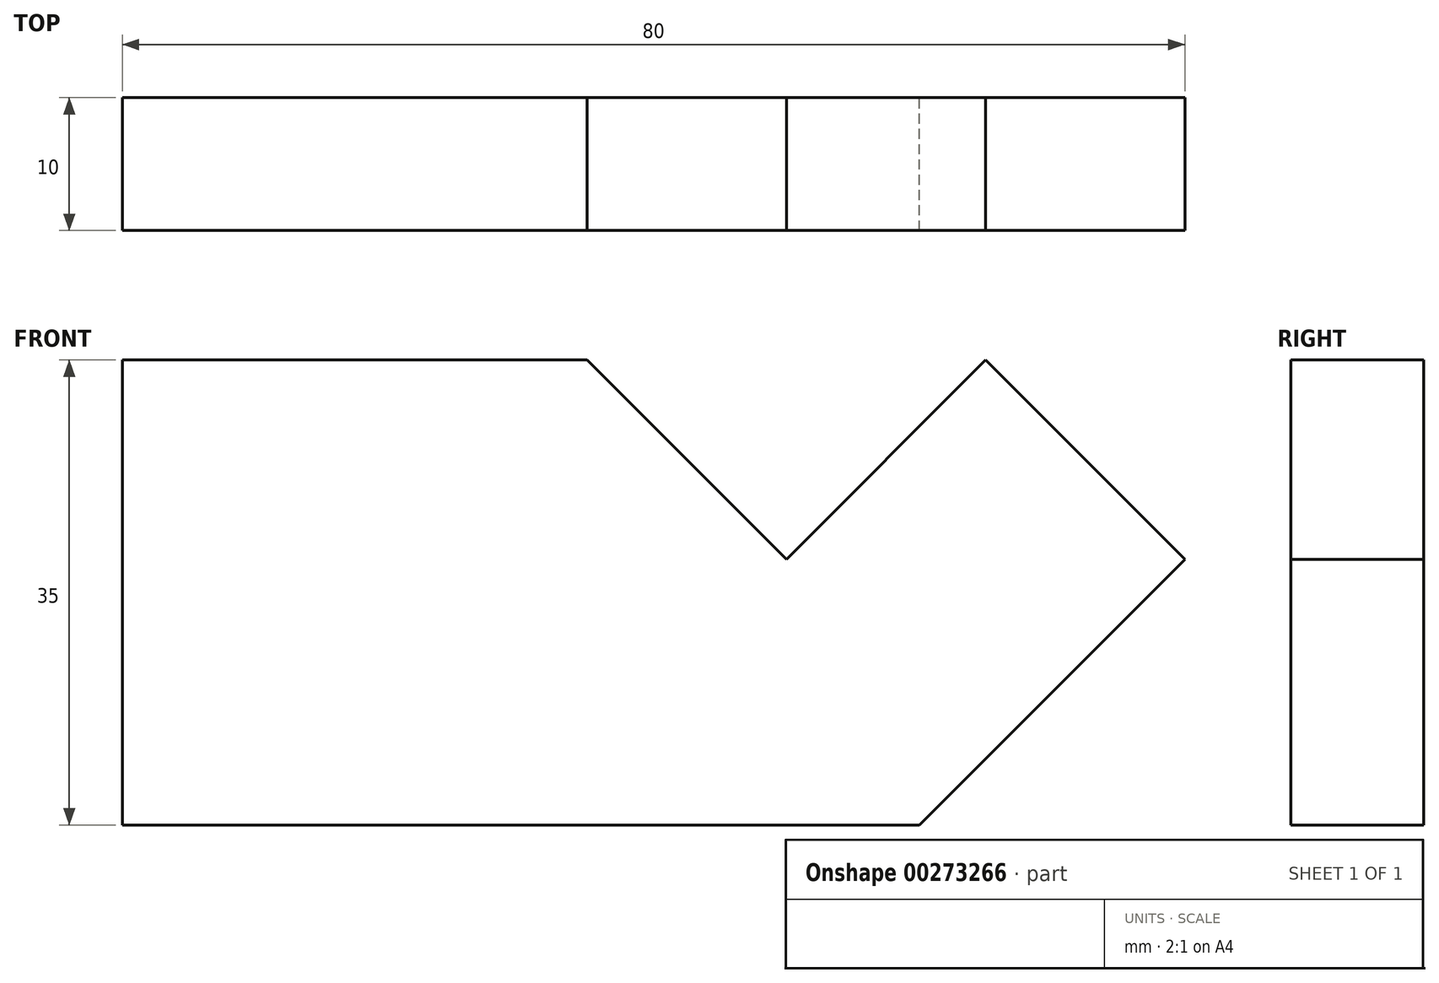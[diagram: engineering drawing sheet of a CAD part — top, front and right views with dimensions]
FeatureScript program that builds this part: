
annotation { "Feature Type Name" : "Feature", "Feature Type Description" : "" }
export const myFeature = defineFeature(function(context is Context, id is Id, definition is map)
    precondition{}
    {
        {
            var Q0;
            Q0=qCreatedBy(makeId("Front.planeOp"),FACE);
            var sketch = newSketch(context, id + "F0", { "sketchPlane" : qUnion([Q0])});
            skLineSegment(sketch, "E0", {"start": v(0, 0) * mm, "end": v(0, 35) * mm});
            skLineSegment(sketch, "E1", {"start": v(0, 35) * mm, "end": v(35, 35) * mm});
            skLineSegment(sketch, "E2", {"start": v(35, 35) * mm, "end": v(50, 20) * mm});
            skLineSegment(sketch, "E3", {"start": v(60, 0) * mm, "end": v(0, 0) * mm});
            skLineSegment(sketch, "E4", {"start": v(50, 20) * mm, "end": v(65, 35) * mm});
            skLineSegment(sketch, "E5", {"start": v(60, 0) * mm, "end": v(80, 20) * mm});
            skLineSegment(sketch, "E6", {"start": v(65, 35) * mm, "end": v(80, 20) * mm});
            skSolve(sketch);
        }
        {
            var Q0;
            Q0 = qSketchRegion(id + "F0", true);
            extrude(context, id + "F1", {"entities" : qUnion([Q0]), "depth" : 10 * mm});
        }
    });
